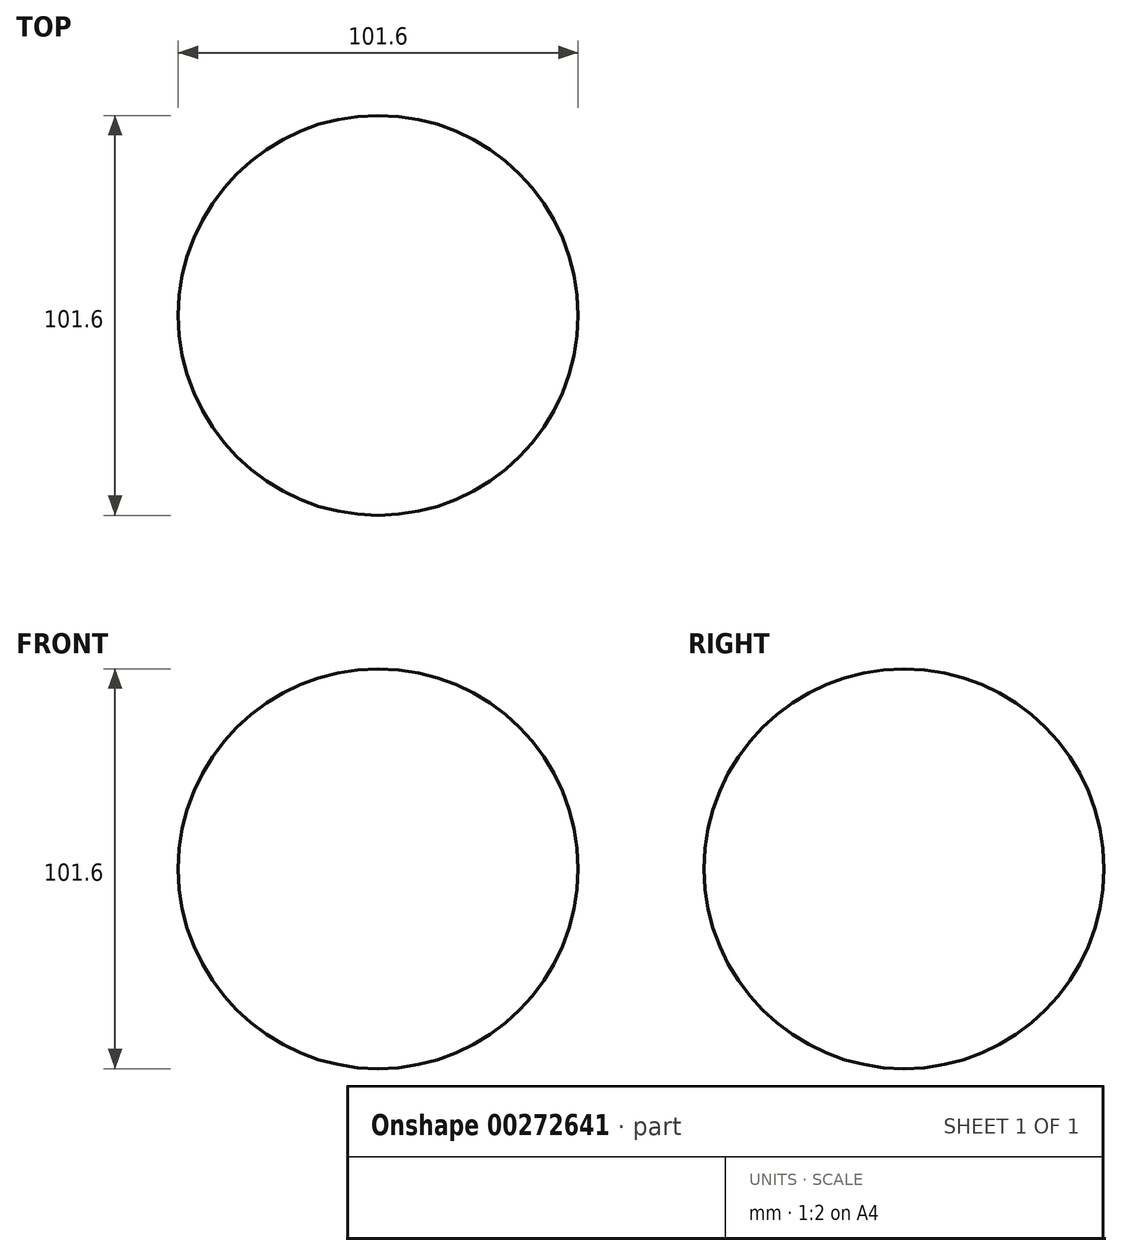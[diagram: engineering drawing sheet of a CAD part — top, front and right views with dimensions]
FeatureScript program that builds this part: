
annotation { "Feature Type Name" : "Feature", "Feature Type Description" : "" }
export const myFeature = defineFeature(function(context is Context, id is Id, definition is map)
    precondition{}
    {
        {
            var Q0;
            Q0=qCreatedBy(makeId("Front.planeOp"),FACE);
            var sketch = newSketch(context, id + "F0", { "sketchPlane" : qUnion([Q0])});
            skArc(sketch, "E0", {"start": v(0, 50.8) * mm, "mid": v(-50.8, 0) * mm, "end": v(0, -50.8) * mm});
            skLineSegment(sketch, "E1", {"start": v(0, 50.8) * mm, "end": v(0, -50.8) * mm});
            skSolve(sketch);
        }
        {
            var Q0;
            Q0=makeQuery(id+"F0.imprint","IMPRINT",FACE,{"disambiguationData":[TD([[makeQuery(id+"F0.imprint","IMPRINT",EDGE,{"derivedFrom":sQuery(id+"F0.wireOp",EDGE,"E0")}),1.0]])]});
            var Q1;
            Q1=sQuery(id+"F0.wireOp",EDGE,"E1");
            revolve(context, id + "F1", {"entities" : qUnion([Q0]), "axis" : qUnion([Q1]), "revolveType" : RevolveType.FULL});
        }
    });
